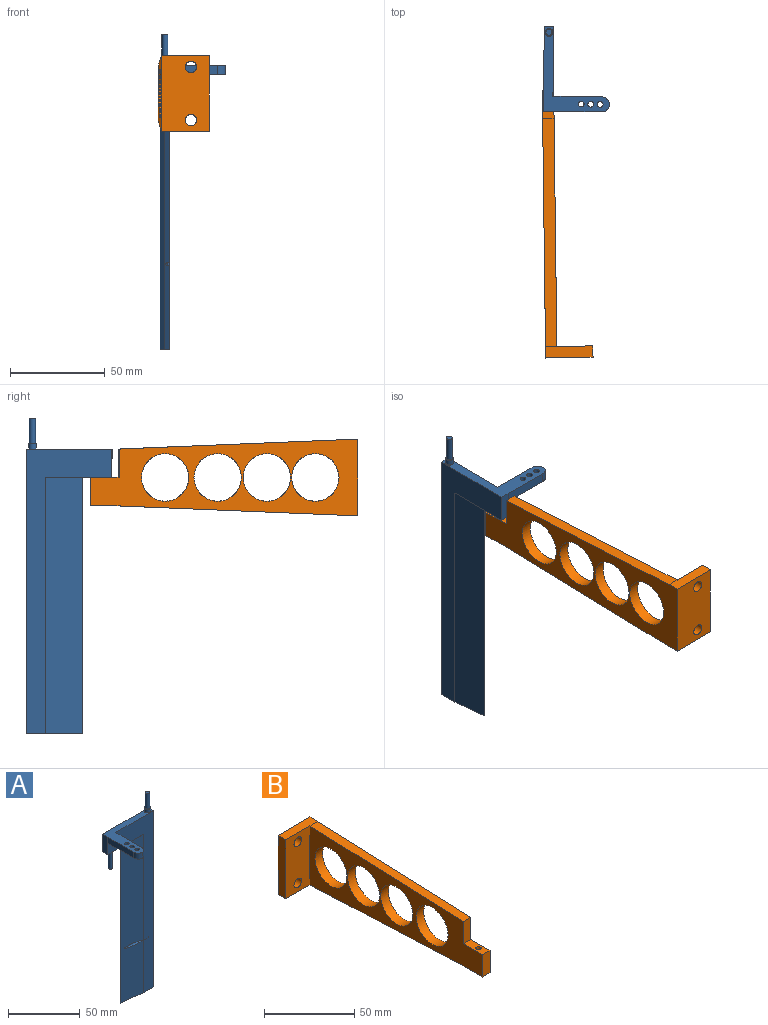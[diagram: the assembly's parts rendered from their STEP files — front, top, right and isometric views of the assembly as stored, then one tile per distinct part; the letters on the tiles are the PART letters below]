
ASSEMBLY  parts=2 mates=1
PART A: 28 faces, bbox 45x35x166.1 mm
  f0: plane 150x45mm, normal (0,-1,0), area 1995.1mm2, adj f2,f4,f5,f6,f11,f12,f20,f21
  f1: cylinder r=1.6mm len=140mm, axis (0,0,1), area 1405.3mm2, adj f8,f9,f10,f19
  f2: plane 135x19.93mm, normal (-0.12,-0.99,0), area 2685.8mm2, adj f0,f3,f5,f9,f11
  f3: plane 135x19.93mm, normal (-0.12,0.99,0), area 2711mm2, adj f2,f5,f7,f11
  f4: plane 45x34.97mm, normal (0,0,1), area 421.4mm2, adj f0,f6,f7,f12,f15,f20,f22,f23
  f5: plane 30x5mm, normal (0,0,-1), area 100.2mm2, adj f0,f2,f3,f6,f7
  f6: plane 150x5mm, normal (1,0,0), area 750mm2, adj f0,f4,f5,f7
  f7: plane 150x45mm, normal (0,1,0), area 2035.1mm2, adj f3,f4,f5,f6,f11,f12
  f8: plane 3.2x3.2mm, normal (0,0,1), area 8mm2, adj f1
  f9: cylinder r=1mm len=22.06mm, axis (-1,0,0), area 88.5mm2, adj f1,f2,f10
  f10: plane 2x1.29mm, normal (-1,0,0), area 2.1mm2, adj f1,f9
  f11: plane 34.93x5mm, normal (0,0,-1), area 118.7mm2, adj f0,f2,f3,f7,f12,f13
  f12: plane 15x5mm, normal (-1,0,0), area 75mm2, adj f0,f4,f7,f11
  f13: cylinder r=1.4mm len=15mm, axis (0,0,1), area 131.9mm2, adj f11,f14
  f14: plane 2.8x2.8mm, normal (0,0,-1), area 6.2mm2, adj f13
  f15: cylinder r=2.09mm len=4.17mm, axis (0,0,-1), area 39.3mm2, adj f4,f16
  f16: plane 4.17x4.17mm, normal (0,0,1), area 5.6mm2, adj f15,f18
  f17: plane 3.2x3.2mm, normal (0,0,1), area 8mm2, adj f18
  f18: cylinder r=1.6mm len=13.1mm, axis (0,0,-1), area 131.6mm2, adj f16,f17
  f19: plane 3.2x3.2mm, normal (0,0,-1), area 8mm2, adj f1
  f20: plane 25.5x5mm, normal (-1,0,0), area 127.5mm2, adj f0,f4,f21,f24
  f21: plane 29.97x8mm, normal (0,0,-1), area 210.1mm2, adj f0,f20,f22,f23,f24,f25,f26,f27
  f22: plane 25.5x5mm, normal (1,0,0), area 127.5mm2, adj f0,f4,f21,f23
  f23: cylinder r=4.5mm len=5mm, axis (0,0,-1), area 32.8mm2, adj f4,f21,f22,f24
  f24: cylinder r=4.5mm len=5mm, axis (0,0,1), area 32.8mm2, adj f4,f20,f21,f23
  f25: cylinder r=1.5mm len=5mm, axis (0,0,1), area 47.1mm2, adj f4,f21
  f26: cylinder r=1.5mm len=5mm, axis (0,0,1), area 47.1mm2, adj f4,f21
  f27: cylinder r=1.5mm len=5mm, axis (0,0,1), area 47.1mm2, adj f4,f21
PART B: 20 faces, bbox 25x141x40 mm
  f0: plane 25x6mm, normal (0,0,1), area 150mm2, adj f3,f5,f6,f9,f15
  f1: plane 25x6mm, normal (0,0,-1), area 150mm2, adj f3,f5,f6,f9,f14
  f2: plane 15x6mm, normal (0,-1,0), area 90mm2, adj f3,f4,f15,f16
  f3: plane 141x40mm, normal (1,0,0), area 2701.5mm2, adj f0,f1,f2,f9,f10,f11,f12,f13
  f4: plane 135x40mm, normal (-1,0,0), area 2461.5mm2, adj f2,f5,f10,f11,f12,f13,f14,f15
  f5: plane 40x19mm, normal (0,-1,0), area 703.5mm2, adj f0,f1,f4,f6,f7,f8
  f6: plane 40x6mm, normal (-1,0,0), area 240mm2, adj f0,f1,f5,f9
  f7: cylinder r=3mm len=6mm, axis (0,1,0), area 113.1mm2, adj f5,f9
  f8: cylinder r=3mm len=6mm, axis (0,1,0), area 113.1mm2, adj f5,f9
  f9: plane 40x25mm, normal (0,1,0), area 943.5mm2, adj f0,f1,f3,f6,f7,f8
  f10: cylinder r=12.5mm len=25mm, axis (-1,0,0), area 471.2mm2, adj f3,f4
  f11: cylinder r=12.5mm len=25mm, axis (-1,0,0), area 471.2mm2, adj f3,f4
  f12: cylinder r=12.5mm len=25mm, axis (-1,0,0), area 471.2mm2, adj f3,f4
  f13: cylinder r=12.5mm len=25mm, axis (-1,0,0), area 471.2mm2, adj f3,f4
  f14: plane 120x6mm, normal (0,-0.04,-1), area 720.6mm2, adj f1,f3,f4,f17
  f15: plane 120x6mm, normal (0,-0.04,1), area 720.6mm2, adj f0,f2,f3,f4
  f16: plane 15x6mm, normal (0,0,1), area 82.9mm2, adj f2,f3,f4,f18,f19
  f17: plane 15x6mm, normal (0,0,-1), area 82.9mm2, adj f3,f4,f14,f18,f19
  f18: plane 15x6mm, normal (0,-1,0), area 90mm2, adj f3,f4,f16,f17
  f19: cylinder r=1.5mm len=15mm, axis (0,0,1), area 141.4mm2, adj f16,f17
PLACE A rot(axis=(0,0,1),89.3deg) t=(138.87,-0.53,91.04)mm
PLACE B rot(axis=(0,0,-1),179.3deg) t=(152.42,-145.39,76.04)mm fixed
MATE revolute B.f19 <-> A.f13  axis (0,0,1) through (141.25,-10.52,76.04)mm
